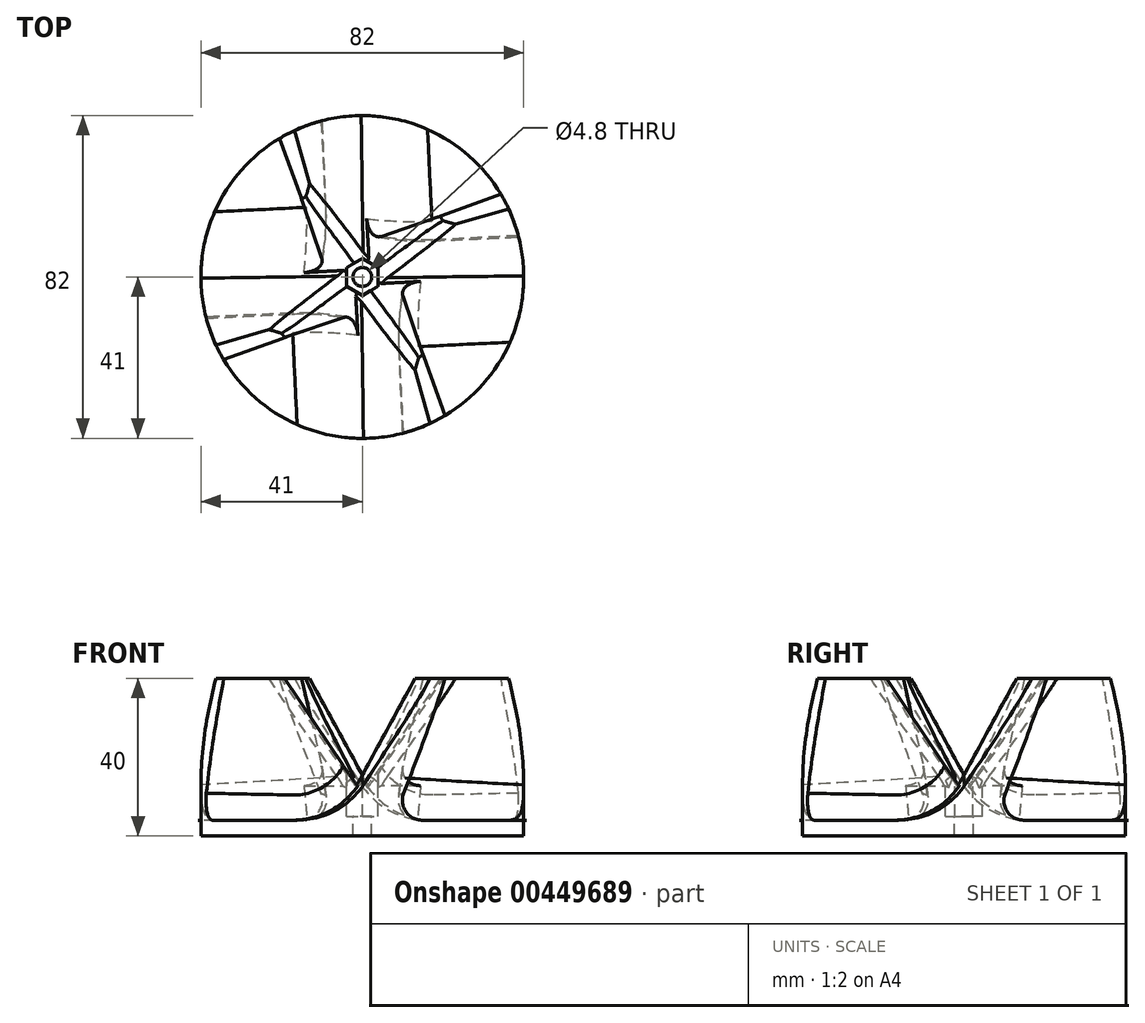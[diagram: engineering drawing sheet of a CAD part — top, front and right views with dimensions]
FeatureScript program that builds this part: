
annotation { "Feature Type Name" : "Feature", "Feature Type Description" : "" }
export const myFeature = defineFeature(function(context is Context, id is Id, definition is map)
    precondition{}
    {
        {
            var Q0;
            Q0=qCreatedBy(makeId("Top.planeOp"),FACE);
            var sketch = newSketch(context, id + "F0", { "sketchPlane" : qUnion([Q0])});
            skLineSegment(sketch, "E0.bottom", {"start": v(7.1, 8.27) * mm, "end": v(-43.93, 8.27) * mm});
            skLineSegment(sketch, "E0.top", {"start": v(7.1, -6.26) * mm, "end": v(-43.93, -6.26) * mm});
            skLineSegment(sketch, "E0.left", {"start": v(7.1, 8.27) * mm, "end": v(7.1, -6.26) * mm});
            skLineSegment(sketch, "E0.right", {"start": v(-43.93, 8.27) * mm, "end": v(-43.93, -6.26) * mm});
            skSolve(sketch);
        }
        {
            var Q0;
            Q0=qCreatedBy(makeId("Top.planeOp"),FACE);
            var sketch = newSketch(context, id + "F1", { "sketchPlane" : qUnion([Q0])});
            skCircle(sketch, "E1", {"center": v(0, 0) * mm, "radius": 41 * mm});
            skCircle(sketch, "E2", {"center": v(0, 0) * mm, "radius": 83.6 * mm});
            skSolve(sketch);
        }
        {
            var Q0;
            Q0=makeQuery(id+"F1.imprint","IMPRINT",FACE,{"disambiguationData":[TD([[makeQuery(id+"F1.imprint","IMPRINT",EDGE,{"derivedFrom":sQuery(id+"F1.wireOp",EDGE,"E1")}),1.0]])]});
            extrude(context, id + "F2", {"entities" : qUnion([Q0]), "depth" : 4 * mm});
        }
        {
            var Q0;
            Q0=qCreatedBy(makeId("Top.planeOp"),FACE);
            cPlane(context, id + "F3", {"entities" : qUnion([Q0]), "cplaneType" : CPlaneType.OFFSET, "offset" : 40 * mm, "width" : 150 * mm, "height" : 150 * mm});
        }
        {
            var Q0;
            Q0=qCreatedBy(id+"F3.planeOp",FACE);
            var sketch = newSketch(context, id + "F4", { "sketchPlane" : qUnion([Q0])});
            skCircle(sketch, "E3", {"center": v(0, 0) * mm, "radius": 25 * mm});
            skCircle(sketch, "E4", {"center": v(0, 0) * mm, "radius": 45 * mm});
            skLineSegment(sketch, "E5", {"start": v(-39.03, -22.4) * mm, "end": v(-19.7, -15.4) * mm});
            skLineSegment(sketch, "E6", {"start": v(-21.49, -12.78) * mm, "end": v(-41.08, -18.37) * mm});
            skCircle(sketch, "E7", {"center": v(0, 0) * mm, "radius": 2.4 * mm});
            skCircle(sketch, "E8.cCircle", {"center": v(0, 0) * mm, "radius": 4.05 * mm, "construction": true});
            skLineSegment(sketch, "E8.0", {"start": v(4.05, 2.34) * mm, "end": v(4.05, -2.34) * mm});
            skLineSegment(sketch, "E8.1", {"start": v(4.05, -2.34) * mm, "end": v(0, -4.68) * mm});
            skLineSegment(sketch, "E8.2", {"start": v(0, -4.68) * mm, "end": v(-4.05, -2.34) * mm});
            skLineSegment(sketch, "E8.3", {"start": v(-4.05, -2.34) * mm, "end": v(-4.05, 2.34) * mm});
            skLineSegment(sketch, "E8.4", {"start": v(-4.05, 2.34) * mm, "end": v(0, 4.68) * mm});
            skLineSegment(sketch, "E8.5", {"start": v(0, 4.68) * mm, "end": v(4.05, 2.34) * mm});
            skPoint(sketch, "E8.0.midPoint", {"position": v(4.05, 0) * mm});
            skSolve(sketch);
        }
        {
            var Q0;
            {var subQ1=sQuery(id+"F4.wireOp",EDGE,"E5");Q0=makeQuery(id+"F4.imprint","IMPRINT",FACE,{"disambiguationData":[TD([[makeQuery(id+"F4.imprint","IMPRINT",EDGE,{"derivedFrom":subQ1}),1.0]])]});}
            var Q1;
            {var subQ0=sQuery(id+"F0.wireOp",EDGE,"E0.left");Q1=makeQuery(id+"F0.imprint","IMPRINT",FACE,{"disambiguationData":[TD([[makeQuery(id+"F0.imprint","IMPRINT",EDGE,{"derivedFrom":subQ0}),-1.0]])]});}
            loft(context, id + "F5", {"sheetProfilesArray" : [{ "sheetProfileEntities" : qUnion([Q0]) }, { "sheetProfileEntities" : qUnion([Q1]) }]});
        }
        {
            var Q0;
            Q0=makeQuery(id+"F5.opLoft","SWEPT_EDGE",EDGE,{"disambiguationData":[OSD([sQuery(id+"F0.wireOp",EDGE,"E0.bottom"),sQuery(id+"F0.wireOp",EDGE,"E0.left"),sQuery(id+"F4.wireOp",EDGE,"E3"),sQuery(id+"F4.wireOp",EDGE,"E6")])]});
            chamfer(context, id + "F6", {"entities" : qUnion([Q0]), "width" : 3 * mm, "tangentPropagation" : true});
        }
        {
            var Q0;
            {var subQ1=sQuery(id+"F0.wireOp",EDGE,"2f4ce80c-512e-42e9-ad37-1b76bf56904e");var subQ4=sQuery(id+"F4.wireOp",EDGE,"E5");Q0=makeQuery(id+"F5.opLoft","SWEPT_BODY",BODY,{"disambiguationData":[OSD([makeQuery(id+"F0.imprint","IMPRINT",FACE,{"disambiguationData":[TD([[makeQuery(id+"F0.imprint","IMPRINT",EDGE,{"derivedFrom":subQ1}),-1.0]])]}),makeQuery(id+"F4.imprint","IMPRINT",FACE,{"disambiguationData":[TD([[makeQuery(id+"F4.imprint","IMPRINT",EDGE,{"derivedFrom":subQ4}),1.0]])]})])]});}
            var Q1;
            Q1=makeQuery(id+"F2.opExtrude","CAP_EDGE",EDGE,{"disambiguationData":[OSD([sQuery(id+"F1.wireOp",EDGE,"E1")])],"isStart":false});
            circularPattern(context, id + "F7", {"entities" : qUnion([Q0]), "axis" : qUnion([Q1]), "angle" : 90 * degree, "instanceCount" : round(4)});
        }
        {
            var Q0;
            {var subQ4=sQuery(id+"F0.wireOp",EDGE,"5ef0fec1-321e-4ed4-9ece-5ae84b4b1e6a.bottom");var subQ6=sQuery(id+"F4.wireOp",EDGE,"E5");Q0=makeQuery(id+"F5.opLoft","SWEPT_BODY",BODY,{"disambiguationData":[OSD([makeQuery(id+"F0.imprint","IMPRINT",FACE,{"disambiguationData":[TD([[makeQuery(id+"F0.imprint","IMPRINT",EDGE,{"derivedFrom":subQ4}),-1.0]])]}),makeQuery(id+"F4.imprint","IMPRINT",FACE,{"disambiguationData":[TD([[makeQuery(id+"F4.imprint","IMPRINT",EDGE,{"derivedFrom":subQ6}),1.0]])]})])]});}
            var Q1;
            {var subQ4=sQuery(id+"F0.wireOp",EDGE,"5ef0fec1-321e-4ed4-9ece-5ae84b4b1e6a.bottom");var subQ6=sQuery(id+"F4.wireOp",EDGE,"E5");Q1=makeQuery(id+"F7.opPattern","COPY",BODY,{"derivedFrom":makeQuery(id+"F5.opLoft","SWEPT_BODY",BODY,{"disambiguationData":[OSD([makeQuery(id+"F0.imprint","IMPRINT",FACE,{"disambiguationData":[TD([[makeQuery(id+"F0.imprint","IMPRINT",EDGE,{"derivedFrom":subQ4}),-1.0]])]}),makeQuery(id+"F4.imprint","IMPRINT",FACE,{"disambiguationData":[TD([[makeQuery(id+"F4.imprint","IMPRINT",EDGE,{"derivedFrom":subQ6}),1.0]])]})])]}),"instanceName":"2"});}
            var Q2;
            {var subQ4=sQuery(id+"F0.wireOp",EDGE,"5ef0fec1-321e-4ed4-9ece-5ae84b4b1e6a.bottom");var subQ6=sQuery(id+"F4.wireOp",EDGE,"E5");Q2=makeQuery(id+"F7.opPattern","COPY",BODY,{"derivedFrom":makeQuery(id+"F5.opLoft","SWEPT_BODY",BODY,{"disambiguationData":[OSD([makeQuery(id+"F0.imprint","IMPRINT",FACE,{"disambiguationData":[TD([[makeQuery(id+"F0.imprint","IMPRINT",EDGE,{"derivedFrom":subQ4}),-1.0]])]}),makeQuery(id+"F4.imprint","IMPRINT",FACE,{"disambiguationData":[TD([[makeQuery(id+"F4.imprint","IMPRINT",EDGE,{"derivedFrom":subQ6}),1.0]])]})])]}),"instanceName":"1"});}
            var Q3;
            {var subQ4=sQuery(id+"F0.wireOp",EDGE,"5ef0fec1-321e-4ed4-9ece-5ae84b4b1e6a.bottom");var subQ6=sQuery(id+"F4.wireOp",EDGE,"E5");Q3=makeQuery(id+"F7.opPattern","COPY",BODY,{"derivedFrom":makeQuery(id+"F5.opLoft","SWEPT_BODY",BODY,{"disambiguationData":[OSD([makeQuery(id+"F0.imprint","IMPRINT",FACE,{"disambiguationData":[TD([[makeQuery(id+"F0.imprint","IMPRINT",EDGE,{"derivedFrom":subQ4}),-1.0]])]}),makeQuery(id+"F4.imprint","IMPRINT",FACE,{"disambiguationData":[TD([[makeQuery(id+"F4.imprint","IMPRINT",EDGE,{"derivedFrom":subQ6}),1.0]])]})])]}),"instanceName":"3"});}
            var Q4;
            Q4=makeQuery(id+"F2.opExtrude","SWEPT_BODY",BODY,{"disambiguationData":[OSD([sQuery(id+"F1.wireOp",EDGE,"E1")])]});
            booleanBodies(context, id + "F8", {"operationType" : BooleanOperationType.UNION, "tools" : qUnion([Q0, Q1, Q2, Q3, Q4])});
        }
        {
            var Q0;
            Q0=makeQuery(id+"F8.opBoolean","INTERSECT",EDGE,{"derivedFrom":[makeQuery(id+"F2.opExtrude","CAP_FACE",FACE,{"disambiguationData":[OSD([sQuery(id+"F1.wireOp",EDGE,"E1")])],"isStart":false}),makeQuery(id+"F5.opLoft","SWEPT_FACE",FACE,{"disambiguationData":[OSD([sQuery(id+"F0.wireOp",EDGE,"E0.bottom"),sQuery(id+"F0.wireOp",EDGE,"E0.left"),sQuery(id+"F0.wireOp",EDGE,"E0.right"),sQuery(id+"F4.wireOp",EDGE,"E3"),sQuery(id+"F4.wireOp",EDGE,"E4"),sQuery(id+"F4.wireOp",EDGE,"E6")])]})]});
            var Q1;
            Q1=makeQuery(id+"F8.opBoolean","INTERSECT",EDGE,{"derivedFrom":[makeQuery(id+"F2.opExtrude","CAP_FACE",FACE,{"disambiguationData":[OSD([sQuery(id+"F1.wireOp",EDGE,"E1")])],"isStart":false}),makeQuery(id+"F7.opPattern","COPY",FACE,{"derivedFrom":makeQuery(id+"F5.opLoft","SWEPT_FACE",FACE,{"disambiguationData":[OSD([sQuery(id+"F0.wireOp",EDGE,"E0.bottom"),sQuery(id+"F0.wireOp",EDGE,"E0.left"),sQuery(id+"F0.wireOp",EDGE,"E0.right"),sQuery(id+"F4.wireOp",EDGE,"E3"),sQuery(id+"F4.wireOp",EDGE,"E4"),sQuery(id+"F4.wireOp",EDGE,"E6")])]}),"instanceName":"3"})]});
            var Q2;
            Q2=makeQuery(id+"F8.opBoolean","INTERSECT",EDGE,{"derivedFrom":[makeQuery(id+"F2.opExtrude","CAP_FACE",FACE,{"disambiguationData":[OSD([sQuery(id+"F1.wireOp",EDGE,"E1")])],"isStart":false}),makeQuery(id+"F7.opPattern","COPY",FACE,{"derivedFrom":makeQuery(id+"F5.opLoft","SWEPT_FACE",FACE,{"disambiguationData":[OSD([sQuery(id+"F0.wireOp",EDGE,"E0.bottom"),sQuery(id+"F0.wireOp",EDGE,"E0.left"),sQuery(id+"F0.wireOp",EDGE,"E0.right"),sQuery(id+"F4.wireOp",EDGE,"E3"),sQuery(id+"F4.wireOp",EDGE,"E4"),sQuery(id+"F4.wireOp",EDGE,"E6")])]}),"instanceName":"1"})]});
            var Q3;
            Q3=makeQuery(id+"F8.opBoolean","INTERSECT",EDGE,{"derivedFrom":[makeQuery(id+"F2.opExtrude","CAP_FACE",FACE,{"disambiguationData":[OSD([sQuery(id+"F1.wireOp",EDGE,"E1")])],"isStart":false}),makeQuery(id+"F7.opPattern","COPY",FACE,{"derivedFrom":makeQuery(id+"F5.opLoft","SWEPT_FACE",FACE,{"disambiguationData":[OSD([sQuery(id+"F0.wireOp",EDGE,"E0.bottom"),sQuery(id+"F0.wireOp",EDGE,"E0.left"),sQuery(id+"F0.wireOp",EDGE,"E0.right"),sQuery(id+"F4.wireOp",EDGE,"E3"),sQuery(id+"F4.wireOp",EDGE,"E4"),sQuery(id+"F4.wireOp",EDGE,"E6")])]}),"instanceName":"2"})]});
            fillet(context, id + "F9", {"entities" : qUnion([Q0, Q1, Q2, Q3]), "radius" : 20 * mm, "tangentPropagation" : true, "allowEdgeOverflow" : false});
        }
        {
            var Q0;
            Q0=makeQuery(id+"F8.opBoolean","INTERSECT",EDGE,{"derivedFrom":[makeQuery(id+"F2.opExtrude","CAP_FACE",FACE,{"disambiguationData":[OSD([sQuery(id+"F1.wireOp",EDGE,"E1")])],"isStart":false}),makeQuery(id+"F5.opLoft","SWEPT_FACE",FACE,{"disambiguationData":[OSD([sQuery(id+"F0.wireOp",EDGE,"E0.top"),sQuery(id+"F0.wireOp",EDGE,"E0.left"),sQuery(id+"F0.wireOp",EDGE,"E0.right"),sQuery(id+"F4.wireOp",EDGE,"E3"),sQuery(id+"F4.wireOp",EDGE,"E4"),sQuery(id+"F4.wireOp",EDGE,"E5")])]})]});
            var Q1;
            Q1=makeQuery(id+"F8.opBoolean","INTERSECT",EDGE,{"derivedFrom":[makeQuery(id+"F2.opExtrude","CAP_FACE",FACE,{"disambiguationData":[OSD([sQuery(id+"F1.wireOp",EDGE,"E1")])],"isStart":false}),makeQuery(id+"F7.opPattern","COPY",FACE,{"derivedFrom":makeQuery(id+"F5.opLoft","SWEPT_FACE",FACE,{"disambiguationData":[OSD([sQuery(id+"F0.wireOp",EDGE,"E0.top"),sQuery(id+"F0.wireOp",EDGE,"E0.left"),sQuery(id+"F0.wireOp",EDGE,"E0.right"),sQuery(id+"F4.wireOp",EDGE,"E3"),sQuery(id+"F4.wireOp",EDGE,"E4"),sQuery(id+"F4.wireOp",EDGE,"E5")])]}),"instanceName":"1"})]});
            var Q2;
            Q2=makeQuery(id+"F8.opBoolean","INTERSECT",EDGE,{"derivedFrom":[makeQuery(id+"F2.opExtrude","CAP_FACE",FACE,{"disambiguationData":[OSD([sQuery(id+"F1.wireOp",EDGE,"E1")])],"isStart":false}),makeQuery(id+"F7.opPattern","COPY",FACE,{"derivedFrom":makeQuery(id+"F5.opLoft","SWEPT_FACE",FACE,{"disambiguationData":[OSD([sQuery(id+"F0.wireOp",EDGE,"E0.top"),sQuery(id+"F0.wireOp",EDGE,"E0.left"),sQuery(id+"F0.wireOp",EDGE,"E0.right"),sQuery(id+"F4.wireOp",EDGE,"E3"),sQuery(id+"F4.wireOp",EDGE,"E4"),sQuery(id+"F4.wireOp",EDGE,"E5")])]}),"instanceName":"2"})]});
            var Q3;
            Q3=makeQuery(id+"F8.opBoolean","INTERSECT",EDGE,{"derivedFrom":[makeQuery(id+"F2.opExtrude","CAP_FACE",FACE,{"disambiguationData":[OSD([sQuery(id+"F1.wireOp",EDGE,"E1")])],"isStart":false}),makeQuery(id+"F7.opPattern","COPY",FACE,{"derivedFrom":makeQuery(id+"F5.opLoft","SWEPT_FACE",FACE,{"disambiguationData":[OSD([sQuery(id+"F0.wireOp",EDGE,"E0.top"),sQuery(id+"F0.wireOp",EDGE,"E0.left"),sQuery(id+"F0.wireOp",EDGE,"E0.right"),sQuery(id+"F4.wireOp",EDGE,"E3"),sQuery(id+"F4.wireOp",EDGE,"E4"),sQuery(id+"F4.wireOp",EDGE,"E5")])]}),"instanceName":"3"})]});
            fillet(context, id + "F10", {"entities" : qUnion([Q0, Q1, Q2, Q3]), "radius" : 5 * mm, "tangentPropagation" : true, "allowEdgeOverflow" : false});
        }
        {
            var Q0;
            Q0=makeQuery(id+"F4.imprint","IMPRINT",FACE,{"disambiguationData":[TD([[makeQuery(id+"F4.imprint","IMPRINT",EDGE,{"derivedFrom":sQuery(id+"F4.wireOp",EDGE,"E7")}),1.0]])]});
            var Q1;
            {var subQ4=sQuery(id+"F0.wireOp",EDGE,"5ef0fec1-321e-4ed4-9ece-5ae84b4b1e6a.bottom");var subQ6=sQuery(id+"F4.wireOp",EDGE,"E5");Q1=makeQuery(id+"F7.opPattern","COPY",BODY,{"derivedFrom":makeQuery(id+"F5.opLoft","SWEPT_BODY",BODY,{"disambiguationData":[OSD([makeQuery(id+"F0.imprint","IMPRINT",FACE,{"disambiguationData":[TD([[makeQuery(id+"F0.imprint","IMPRINT",EDGE,{"derivedFrom":subQ4}),-1.0]])]}),makeQuery(id+"F4.imprint","IMPRINT",FACE,{"disambiguationData":[TD([[makeQuery(id+"F4.imprint","IMPRINT",EDGE,{"derivedFrom":subQ6}),1.0]])]})])]}),"instanceName":"2"});}
            extrude(context, id + "F11", {"entities" : qUnion([Q0]), "operationType" : NewBodyOperationType.REMOVE, "endBound" : BoundingType.THROUGH_ALL, "oppositeDirection" : true, "endBoundEntityBody" : qUnion([Q1]), "depth" : 25 * mm});
        }
        {
            var Q0;
            Q0=makeQuery(id+"F4.imprint","IMPRINT",FACE,{"disambiguationData":[TD([[makeQuery(id+"F4.imprint","IMPRINT",EDGE,{"derivedFrom":sQuery(id+"F4.wireOp",EDGE,"E7")}),-1.0]])]});
            extrude(context, id + "F12", {"entities" : qUnion([Q0]), "operationType" : NewBodyOperationType.REMOVE, "oppositeDirection" : true, "depth" : 35 * mm});
        }
        {
            var Q0;
            Q0=makeQuery(id+"F1.imprint","IMPRINT",FACE,{"disambiguationData":[TD([[makeQuery(id+"F1.imprint","IMPRINT",EDGE,{"derivedFrom":sQuery(id+"F1.wireOp",EDGE,"E1")}),-1.0]])]});
            extrude(context, id + "F13", {"entities" : qUnion([Q0]), "operationType" : NewBodyOperationType.REMOVE, "depth" : 50 * mm});
        }
    });
